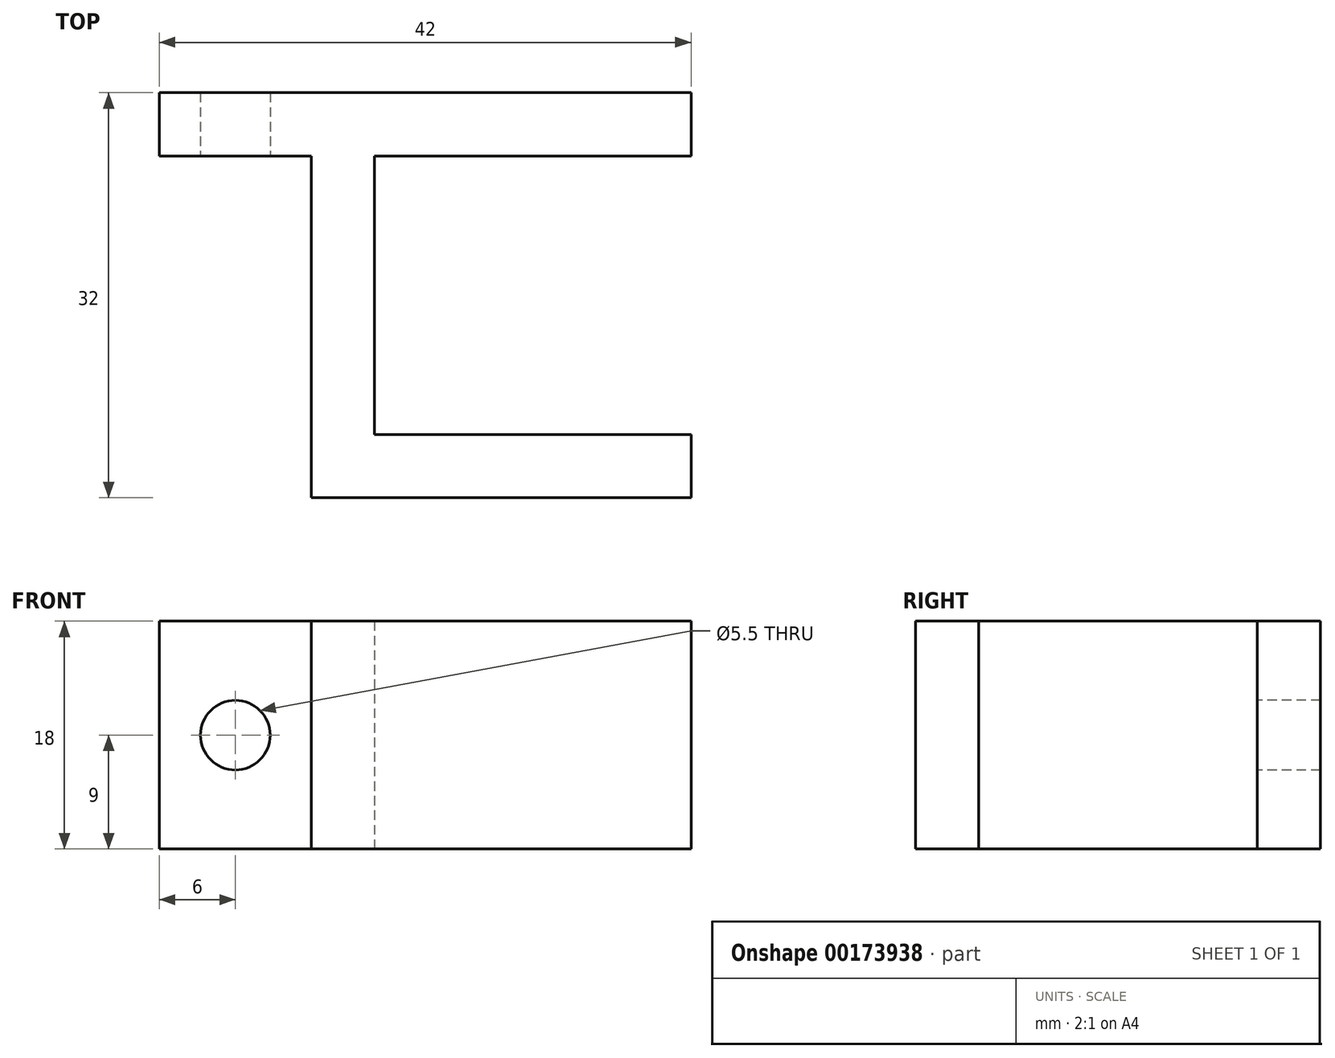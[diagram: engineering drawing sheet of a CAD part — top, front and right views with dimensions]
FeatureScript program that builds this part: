
annotation { "Feature Type Name" : "Feature", "Feature Type Description" : "" }
export const myFeature = defineFeature(function(context is Context, id is Id, definition is map)
    precondition{}
    {
        {
            var Q0;
            Q0=qCreatedBy(makeId("Top.planeOp"),FACE);
            var sketch = newSketch(context, id + "F0", { "sketchPlane" : qUnion([Q0])});
            skLineSegment(sketch, "E0.bottom", {"start": v(0, 0) * mm, "end": v(42, 0) * mm});
            skLineSegment(sketch, "E0.top", {"start": v(0, 5) * mm, "end": v(42, 5) * mm});
            skLineSegment(sketch, "E0.left", {"start": v(0, 0) * mm, "end": v(0, 5) * mm});
            skLineSegment(sketch, "E0.right", {"start": v(42, 0) * mm, "end": v(42, 5) * mm});
            skLineSegment(sketch, "E1.bottom", {"start": v(12, 0) * mm, "end": v(17, 0) * mm});
            skLineSegment(sketch, "E1.top", {"start": v(12, -27) * mm, "end": v(17, -27) * mm});
            skLineSegment(sketch, "E1.left", {"start": v(12, 0) * mm, "end": v(12, -27) * mm});
            skLineSegment(sketch, "E1.right", {"start": v(17, 0) * mm, "end": v(17, -27) * mm});
            skLineSegment(sketch, "E2.bottom", {"start": v(17, -27) * mm, "end": v(42, -27) * mm});
            skLineSegment(sketch, "E2.top", {"start": v(17, -22) * mm, "end": v(42, -22) * mm});
            skLineSegment(sketch, "E2.left", {"start": v(17, -27) * mm, "end": v(17, -22) * mm});
            skLineSegment(sketch, "E2.right", {"start": v(42, -27) * mm, "end": v(42, -22) * mm});
            skSolve(sketch);
        }
        {
            var Q0;
            Q0 = qSketchRegion(id + "F0", true);
            extrude(context, id + "F1", {"entities" : qUnion([Q0]), "depth" : 18 * mm, "offsetDistance" : 25 * mm});
        }
        {
            var Q0;
            {var subQ0=sQuery(id+"F0.wireOp",EDGE,"E0.bottom");Q0=makeQuery(id+"F1.opExtrude","SWEPT_FACE",FACE,{"disambiguationData":[OSD([subQ0]),TDD([makeQuery(id+"F0.imprint","IMPRINT",EDGE,{"disambiguationData":[TD([[makeQuery(id+"F0.imprint","INTERSECT",VERTEX,{"derivedFrom":[subQ0,sQuery(id+"F0.wireOp",EDGE,"E0.left")]}),-1.0]])],"derivedFrom":subQ0})])]});}
            var sketch = newSketch(context, id + "F2", { "sketchPlane" : qUnion([Q0])});
            skLineSegment(sketch, "E3.bottom", {"start": v(12, 18) * mm, "end": v(0, 18) * mm});
            skLineSegment(sketch, "E3.top", {"start": v(12, 0) * mm, "end": v(0, 0) * mm});
            skLineSegment(sketch, "E3.left", {"start": v(12, 18) * mm, "end": v(12, 0) * mm});
            skLineSegment(sketch, "E3.right", {"start": v(0, 18) * mm, "end": v(0, 0) * mm});
            skPoint(sketch, "E3.middle", {"position": v(6, 9) * mm});
            skPoint(sketch, "E3.middle.positionSnap0", {"position": v(12, 9) * mm});
            skPoint(sketch, "E3.centerSnap0", {"position": v(12, 9) * mm});
            skSolve(sketch);
        }
        {
            var Q0;
            Q0=sQuery(id+"F2.wireOp",VERTEX,"E3.middle");
            var Q1;
            Q1=makeQuery(id+"F1.opExtrude","SWEPT_BODY",BODY,{"disambiguationData":[OSD([sQuery(id+"F0.wireOp",EDGE,"E0.bottom"),sQuery(id+"F0.wireOp",EDGE,"E0.top"),sQuery(id+"F0.wireOp",EDGE,"E0.left"),sQuery(id+"F0.wireOp",EDGE,"E0.right"),sQuery(id+"F0.wireOp",EDGE,"E1.top"),sQuery(id+"F0.wireOp",EDGE,"E1.left"),sQuery(id+"F0.wireOp",EDGE,"E1.right"),sQuery(id+"F0.wireOp",EDGE,"E2.bottom"),sQuery(id+"F0.wireOp",EDGE,"E2.top"),sQuery(id+"F0.wireOp",EDGE,"E2.right")])]});
            hole(context, id + "F3", {"style" : HoleStyle.SIMPLE, "endStyle" : HoleEndStyle.BLIND, "standardTappedOrClearance" : lookupTablePath({ "fit" : "Normal", "standard" : "ISO", "size" : "M5", "type" : "Clearance" }), "standardBlindInLast" : lookupTablePath({ "fit" : "Normal", "standard" : "ISO", "engagement" : "75%", "pitch" : "0.8 mm", "size" : "M5", "type" : "Clearance & tapped" }), "holeDiameter" : 5.5 * mm, "majorDiameter" : 5 * mm, "holeDepth" : 10 * mm, "tappedDepth" : 12 * mm, "tapClearance" : 3, "locations" : qUnion([Q0]), "scope" : qUnion([Q1])});
        }
    });
